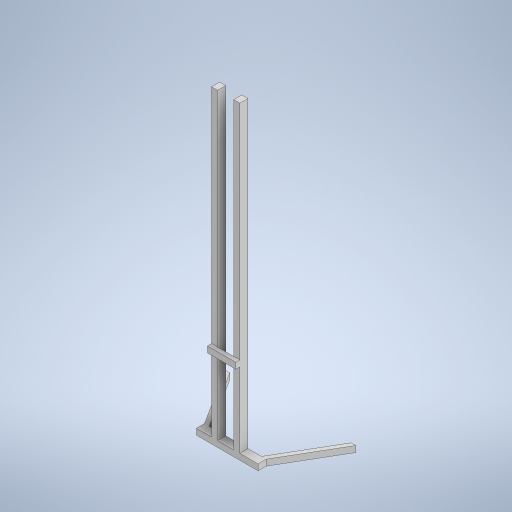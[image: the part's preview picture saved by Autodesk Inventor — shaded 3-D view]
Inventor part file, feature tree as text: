
AUTODESK INVENTOR PART (.ipt)
format: ipt  version: 2023 (Build 270158000, 158)  size: 295,936 bytes
history: native  units: mm
features: extrude x3, sketch x3, other x1
ambient origin geometry x8: Origin, YZ Plane, XZ Plane, XY Plane, X Axis, Y Axis, Z Axis, Center Point
bodies: Body1 (feature_tree)
feature tree (7):
  other  "Твердое тело1"
  extrude  "Выдавливание1"  Depth=110.0mm
  extrude  "Выдавливание2"  Depth=15.0mm
  extrude  "Выдавливание3"  Depth=30.0mm
  sketch  "Эскиз1"
  sketch  "Эскиз2"
  sketch  "Эскиз3"
